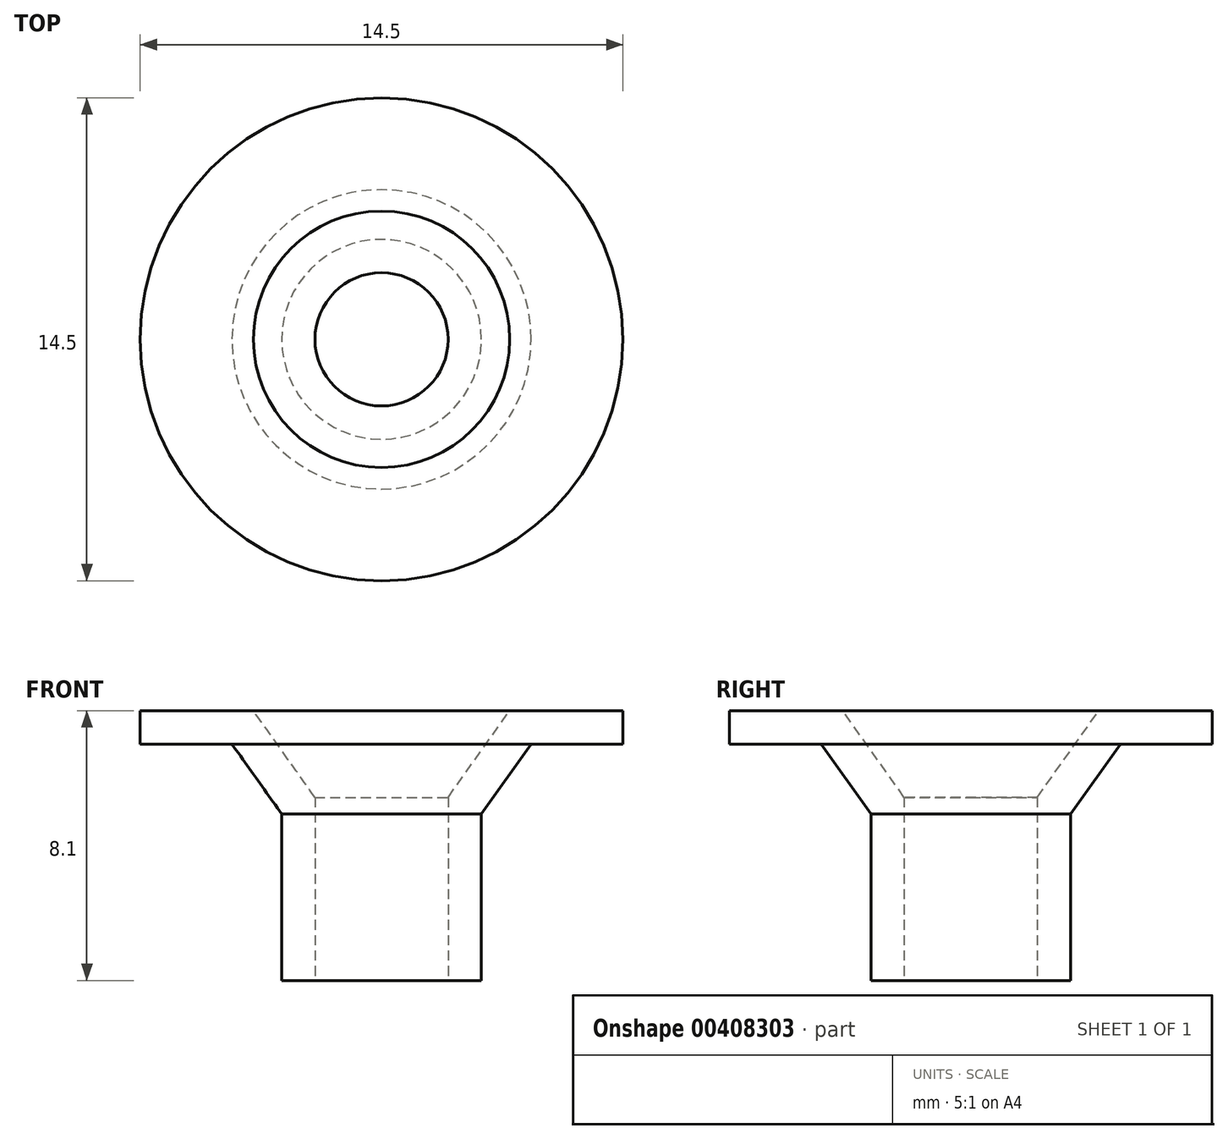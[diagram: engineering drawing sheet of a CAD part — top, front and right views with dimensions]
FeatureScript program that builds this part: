
annotation { "Feature Type Name" : "Feature", "Feature Type Description" : "" }
export const myFeature = defineFeature(function(context is Context, id is Id, definition is map)
    precondition{}
    {
        {
            var Q0;
            Q0=qCreatedBy(makeId("Front.planeOp"),FACE);
            var sketch = newSketch(context, id + "F0", { "sketchPlane" : qUnion([Q0])});
            skLineSegment(sketch, "E0", {"start": v(2, 0) * mm, "end": v(2, 5.5) * mm});
            skLineSegment(sketch, "E1", {"start": v(2, 5.5) * mm, "end": v(3.85, 8.1) * mm});
            skLineSegment(sketch, "E2", {"start": v(3.85, 8.1) * mm, "end": v(7.25, 8.1) * mm});
            skLineSegment(sketch, "E3", {"start": v(7.25, 8.1) * mm, "end": v(7.25, 7.1) * mm});
            skLineSegment(sketch, "E4", {"start": v(7.25, 7.1) * mm, "end": v(4.5, 7.1) * mm});
            skLineSegment(sketch, "E5", {"start": v(4.5, 7.1) * mm, "end": v(3, 5) * mm});
            skLineSegment(sketch, "E6", {"start": v(3, 5) * mm, "end": v(3, 0) * mm});
            skLineSegment(sketch, "E7", {"start": v(3, 0) * mm, "end": v(2, 0) * mm});
            skLineSegment(sketch, "E8", {"start": v(0, 0) * mm, "end": v(0, 8.1) * mm, "construction": true});
            skLineSegment(sketch, "E9", {"start": v(0, 8.1) * mm, "end": v(3.85, 8.1) * mm, "construction": true});
            skSolve(sketch);
        }
        {
            var Q0;
            Q0 = qSketchRegion(id + "F0", true);
            var Q1;
            Q1=sQuery(id+"F0.wireOp",EDGE,"E8");
            revolve(context, id + "F1", {"entities" : qUnion([Q0]), "axis" : qUnion([Q1]), "revolveType" : RevolveType.FULL});
        }
    });
